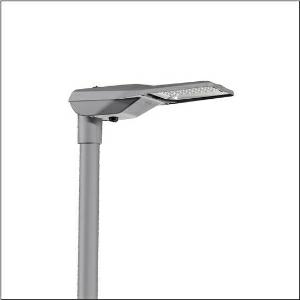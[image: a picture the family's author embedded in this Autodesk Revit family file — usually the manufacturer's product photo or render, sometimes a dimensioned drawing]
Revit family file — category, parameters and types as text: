
# Revit family: streetlight_sl_21_mini___st1_5a_5xe2p33t08gb_e3d2
name_source: partatom
category: Lighting Fixtures
units: mm (PartAtom-declared; Revit-internal decimal feet)

## family parameters
Cut with Voids When Loaded = No
Host = Face
Light Source = No
Part Type = Normal
Room Calculation Point = No
Round Connector Dimension = Use Diameter
Shared = No

## types (1)
- --- (1 x LED, 5840 lm, 40.4 W, 3000K)
    Apparent Load = 40 VA
    CIE Flux Codes = 22 53 95 100 100
    Color Rendering = 70
    Color Temperature = 3000K
    Default Elevation = 1800 mm
    Description = Streetlight SL 21 mini, mast luminaire, primary light control with lens, of PMMA, primary optical cover: cover, of toughened safety glass, transparent, light distribution: ST1.5a, light emission: direct distribution, primary light characteristic: asymmetric, installation type: side-entry, post-top, LED, High Power LED, rated luminous flux: 5.840lm, luminous efficacy: 145lm/W, light colour: 730, colour temperature: 3000K, control gear: D4i, control: overheat protection, constant luminous flux control, time-dependent luminous flux control, flexible luminous flux parameterisation, pre-setting: logarithmic dimming characteristic, mains connection: 220..240V, AC, 50/60Hz, start of lifetime: 40W, end of service life: 41W, reduction: 19W, luminaire housing, of diecast aluminium, powder-coated, SITECO metallic grey (DB 702S), corrosivity category C5 high according to DIN EN ISO 12944, please order mast flange separately, inclination adjustable: 0°, 5°, 10°, 15°, sealing non-destructively replaceable, multi-level sealing system, length: 628mm, width: 235mm, height: 110mm, mast flange for spigot size: 42mm (side-entry): 5XC10008XM4, 60/48mm (side-entry/post-top): 5XC10108XM2, 76/60mm (side-entry/post-top): 5XC10108XM1, mounting height: 4..8m, Smart Interface below and above, protection rating (complete): IP66, insulation class (complete): insulation class II (safety insulation), certification: CE, ENEC, ENEC+, VDE, impact resistance: IK10, permissible operating ambient temperature for outdoor applications: -40..+50°C, standard-compliant lighting for roads and squares, packaging unit: 1 piece

Light Distribution: ST1.5a
    Height = 110 mm
    Lamp = 1 x LED
    Lamp Light Flux = 5840 lm
    Lamp Power = 40.4 W
    Lamp count = 1
    Length = 625 mm
    Luminous efficacy = 145 lm/W
    Manufacturer = Siteco
    ModVariant = No
    Model = 5XE2P33T08GB
    Number of Poles = 1
    OnlyDefault = Yes
    Power Factor = 1
    Product Name = Streetlight SL 21 mini | ST1.5a
    Product group = mast luminaire | pylon top
    ProductGroupID = 6100
    Protection Class = Protection class II
    Protection Degree = IP 66
    RLX_Detail_Level = 1
    RLX_Emergency_Light_Flux = 0 lm
    RLX_Emergency_Type = 0
    RLX_Emergency_Type_DB = No
    RlxData = <blob elided: 29873 chars, md5=59093ee1>
    Socket = socket
    Standby Power = 0 W
    System Light Flux = 5840 lm
    System Power = 40 W
    Type Comments = factory setting: luminous flux: 100 % | dim-lin: 254 | 812 mA
    Type Image = l_1003514.jpg
    URL = http://relux.com
    VarID = @adj_175051
    Voltage = 0 V
    Weight = 0.00 kg
    Width = 234 mm

## geometry (parser evidence)
native form markers: Blend x4, Sweep x10
no freeform markers — native parametric forms only
